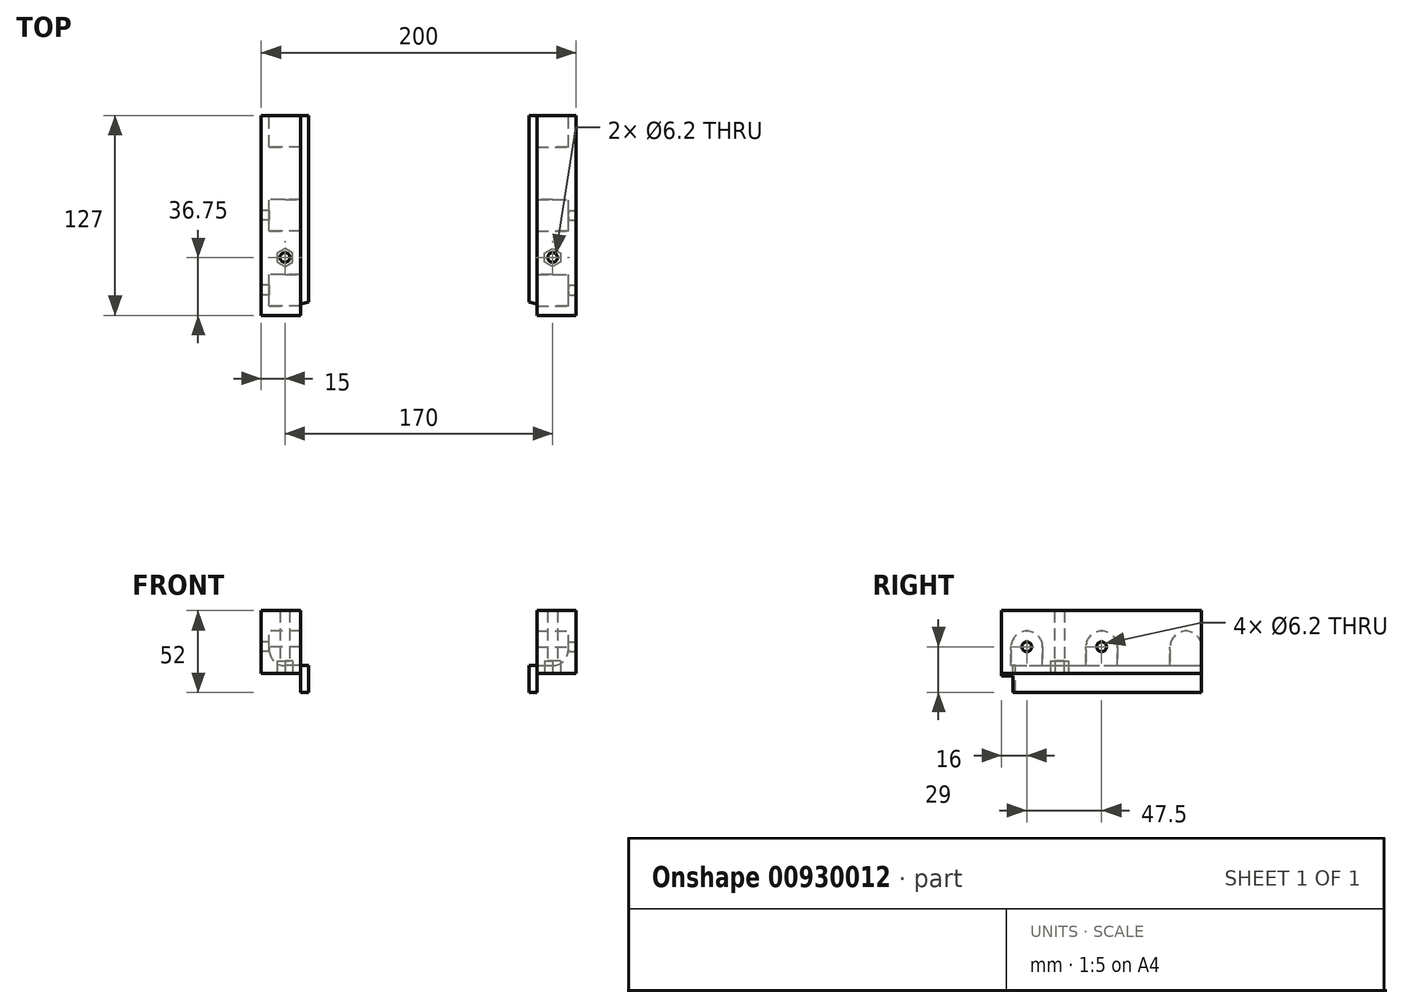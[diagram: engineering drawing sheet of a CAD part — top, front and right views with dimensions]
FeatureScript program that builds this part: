
annotation { "Feature Type Name" : "Feature", "Feature Type Description" : "" }
export const myFeature = defineFeature(function(context is Context, id is Id, definition is map)
    precondition{}
    {
        {
            var Q0;
            Q0=qCreatedBy(makeId("Front.planeOp"),FACE);
            var sketch = newSketch(context, id + "F0", { "sketchPlane" : qUnion([Q0])});
            skLineSegment(sketch, "E0", {"start": v(0, 40) * mm, "end": v(0, 0) * mm});
            skLineSegment(sketch, "E1", {"start": v(0, 0) * mm, "end": v(23.5, 0) * mm});
            skLineSegment(sketch, "E2", {"start": v(25, -1.5) * mm, "end": v(25, -12) * mm});
            skLineSegment(sketch, "E3", {"start": v(25, -12) * mm, "end": v(30, -12) * mm});
            skLineSegment(sketch, "E4", {"start": v(30, -12) * mm, "end": v(30, 5) * mm});
            skLineSegment(sketch, "E5", {"start": v(30, 5) * mm, "end": v(15, 5) * mm});
            skLineSegment(sketch, "E6", {"start": v(5, 15) * mm, "end": v(5, 40) * mm});
            skLineSegment(sketch, "E7", {"start": v(5, 40) * mm, "end": v(0, 40) * mm});
            skPoint(sketch, "E8.visualSharp", {"position": v(25, 0) * mm});
            skArc(sketch, "E8.filletArc", {"start": v(25, -1.5) * mm, "mid": v(24.56, -0.44) * mm, "end": v(23.5, 0) * mm});
            skPoint(sketch, "E9.visualSharp", {"position": v(5, 5) * mm});
            skArc(sketch, "E9.filletArc", {"start": v(5, 15) * mm, "mid": v(7.93, 7.93) * mm, "end": v(15, 5) * mm});
            skSolve(sketch);
        }
        {
            var Q0;
            Q0=makeQuery(id+"F0.imprint","IMPRINT",FACE,{"disambiguationData":[TD([[makeQuery(id+"F0.imprint","IMPRINT",EDGE,{"derivedFrom":sQuery(id+"F0.wireOp",EDGE,"E0")}),1.0]])]});
            extrude(context, id + "F1", {"entities" : qUnion([Q0]), "endBound" : BoundingType.SYMMETRIC, "depth" : 127 * mm, "offsetDistance" : 25 * mm});
        }
        {
            var Q0;
            Q0=makeQuery(id+"F1.opExtrude","SWEPT_FACE",FACE,{"disambiguationData":[OSD([sQuery(id+"F0.wireOp",EDGE,"E0")])]});
            var sketch = newSketch(context, id + "F2", { "sketchPlane" : qUnion([Q0])});
            skPoint(sketch, "E10", {"position": v(0, 17) * mm});
            skPoint(sketch, "E11", {"position": v(47.5, 17) * mm});
            skPoint(sketch, "E12", {"position": v(-53.5, 17) * mm});
            skSolve(sketch);
        }
        {
            var Q0;
            {var subQ0=sQuery(id+"F0.wireOp",EDGE,"E0");Q0=makeQuery(id+"F2.imprint","IMPRINT",FACE,{"disambiguationData":[TD([[makeQuery(id+"F2.imprint","IMPRINT",EDGE,{"derivedFrom":makeQuery(id+"F1.opExtrude","CAP_EDGE",EDGE,{"disambiguationData":[OSD([subQ0])],"isStart":true})}),1.0]])]});}
            var sketch = newSketch(context, id + "F3", { "sketchPlane" : qUnion([Q0])});
            skArc(sketch, "E13", {"start": v(-10, 17) * mm, "mid": v(0, 27) * mm, "end": v(10, 17) * mm});
            skArc(sketch, "E14", {"start": v(37.5, 17) * mm, "mid": v(47.5, 27) * mm, "end": v(57.5, 17) * mm});
            skLineSegment(sketch, "E15", {"start": v(-10, 17) * mm, "end": v(-10, 0) * mm});
            skLineSegment(sketch, "E16", {"start": v(-10, 0) * mm, "end": v(10, 0) * mm});
            skLineSegment(sketch, "E17", {"start": v(10, 0) * mm, "end": v(10, 17) * mm});
            skLineSegment(sketch, "E18", {"start": v(37.5, 17) * mm, "end": v(37.5, 0) * mm});
            skLineSegment(sketch, "E19", {"start": v(37.5, 0) * mm, "end": v(57.5, 0) * mm});
            skLineSegment(sketch, "E20", {"start": v(57.5, 0) * mm, "end": v(57.5, 17) * mm});
            skArc(sketch, "E21", {"start": v(-63.5, 17) * mm, "mid": v(-53.5, 27) * mm, "end": v(-43.5, 17) * mm});
            skLineSegment(sketch, "E22", {"start": v(-63.5, 17) * mm, "end": v(-63.5, 0) * mm});
            skLineSegment(sketch, "E23", {"start": v(-63.5, 0) * mm, "end": v(-43.5, 0) * mm});
            skLineSegment(sketch, "E24", {"start": v(-43.5, 0) * mm, "end": v(-43.5, 17) * mm});
            skSolve(sketch);
        }
        {
            var Q0;
            Q0=makeQuery(id+"F3.imprint","IMPRINT",FACE,{"disambiguationData":[TD([[makeQuery(id+"F3.imprint","IMPRINT",EDGE,{"derivedFrom":sQuery(id+"F3.wireOp",EDGE,"E14")}),-1.0]])]});
            var Q1;
            Q1=makeQuery(id+"F3.imprint","IMPRINT",FACE,{"disambiguationData":[TD([[makeQuery(id+"F3.imprint","IMPRINT",EDGE,{"derivedFrom":sQuery(id+"F3.wireOp",EDGE,"E13")}),-1.0]])]});
            var Q2;
            Q2=makeQuery(id+"F3.imprint","IMPRINT",FACE,{"disambiguationData":[TD([[makeQuery(id+"F3.imprint","IMPRINT",EDGE,{"derivedFrom":sQuery(id+"F3.wireOp",EDGE,"E21")}),-1.0]])]});
            var Q3;
            Q3=makeQuery(id+"F1.opExtrude","SWEPT_FACE",FACE,{"disambiguationData":[OSD([sQuery(id+"F0.wireOp",EDGE,"E4")])]});
            extrude(context, id + "F4", {"entities" : qUnion([Q0, Q1, Q2]), "operationType" : NewBodyOperationType.ADD, "oppositeDirection" : true, "depth" : 25 * mm, "endBoundEntityFace" : qUnion([Q3]), "offsetDistance" : 25 * mm});
        }
        {
            var Q0;
            Q0=sQuery(id+"F2.wireOp",VERTEX,"E10");
            var Q1;
            Q1=sQuery(id+"F2.wireOp",VERTEX,"E11");
            var Q2;
            Q2=makeQuery(id+"F1.opExtrude","SWEPT_BODY",BODY,{"disambiguationData":[OSD([sQuery(id+"F0.wireOp",EDGE,"E0"),sQuery(id+"F0.wireOp",EDGE,"E1"),sQuery(id+"F0.wireOp",EDGE,"E2"),sQuery(id+"F0.wireOp",EDGE,"E3"),sQuery(id+"F0.wireOp",EDGE,"E4"),sQuery(id+"F0.wireOp",EDGE,"E5"),sQuery(id+"F0.wireOp",EDGE,"E6"),sQuery(id+"F0.wireOp",EDGE,"E7"),sQuery(id+"F0.wireOp",EDGE,"E8.filletArc"),sQuery(id+"F0.wireOp",EDGE,"E9.filletArc")])]});
            hole(context, id + "F5", {"style" : HoleStyle.SIMPLE, "endStyle" : HoleEndStyle.THROUGH, "holeDiameter" : 6.2 * mm, "majorDiameter" : 5 * mm, "isTappedThrough" : true, "tappedDepth" : 12 * mm, "tapClearance" : 3, "locations" : qUnion([Q0, Q1]), "scope" : qUnion([Q2])});
        }
        {
            var Q0;
            Q0=makeQuery(id+"F1.opExtrude","SWEPT_FACE",FACE,{"disambiguationData":[OSD([sQuery(id+"F0.wireOp",EDGE,"E1")])]});
            var sketch = newSketch(context, id + "F6", { "sketchPlane" : qUnion([Q0])});
            skPoint(sketch, "E25", {"position": v(15, 26.75) * mm});
            skSolve(sketch);
        }
        {
            var Q0;
            {var subQ0=sQuery(id+"F0.wireOp",EDGE,"E1");Q0=makeQuery(id+"F6.imprint","IMPRINT",FACE,{"disambiguationData":[TD([[makeQuery(id+"F6.imprint","IMPRINT",EDGE,{"derivedFrom":makeQuery(id+"F1.opExtrude","CAP_EDGE",EDGE,{"disambiguationData":[OSD([subQ0])],"isStart":true})}),1.0]])]});}
            var sketch = newSketch(context, id + "F7", { "sketchPlane" : qUnion([Q0])});
            skArc(sketch, "E26", {"start": v(15, 16.75) * mm, "mid": v(25, 26.75) * mm, "end": v(15, 36.75) * mm});
            skLineSegment(sketch, "E27", {"start": v(15, 36.75) * mm, "end": v(0, 36.75) * mm});
            skLineSegment(sketch, "E28", {"start": v(0, 36.75) * mm, "end": v(0, 16.75) * mm});
            skLineSegment(sketch, "E29", {"start": v(0, 16.75) * mm, "end": v(15, 16.75) * mm});
            skSolve(sketch);
        }
        {
            var Q0;
            {var subQ0=sQuery(id+"F7.wireOp",EDGE,"E27");Q0=makeQuery(id+"F7.imprint","IMPRINT",FACE,{"disambiguationData":[TD([[makeQuery(id+"F7.imprint","IMPRINT",EDGE,{"derivedFrom":subQ0}),1.0]])]});}
            var Q1;
            {var subQ0=sQuery(id+"F7.wireOp",EDGE,"E26");var subQ1=makeQuery(id+"F6.imprint","IMPRINT",EDGE,{"derivedFrom":makeQuery(id+"F4.boolean.opBoolean","INTERSECT",EDGE,{"derivedFrom":[makeQuery(id+"F4.opExtrude","SWEPT_FACE",FACE,{"disambiguationData":[OSD([sQuery(id+"F3.wireOp",EDGE,"E16")])]}),makeQuery(id+"F4.opExtrude","SWEPT_FACE",FACE,{"disambiguationData":[OSD([sQuery(id+"F3.wireOp",EDGE,"E19")])]})]})});var subQ2=makeQuery(id+"F7.imprint","INTERSECT",VERTEX,{"disambiguationData":[OD(0.0)],"derivedFrom":[subQ1,subQ0]});Q1=makeQuery(id+"F7.imprint","IMPRINT",FACE,{"disambiguationData":[TD([[makeQuery(id+"F7.imprint","IMPRINT",EDGE,{"disambiguationData":[TD([[subQ2,-1.0]])],"derivedFrom":subQ0}),1.0]])]});}
            var Q2;
            Q2=makeQuery(id+"F1.opExtrude","SWEPT_FACE",FACE,{"disambiguationData":[OSD([sQuery(id+"F0.wireOp",EDGE,"E7")])]});
            extrude(context, id + "F8", {"entities" : qUnion([Q0, Q1]), "operationType" : NewBodyOperationType.ADD, "oppositeDirection" : true, "depth" : 30 * mm, "endBoundEntityFace" : qUnion([Q2]), "offsetDistance" : 25 * mm});
        }
        {
            var Q0;
            Q0=sQuery(id+"F6.wireOp",VERTEX,"E25");
            var Q1;
            Q1=makeQuery(id+"F1.opExtrude","SWEPT_BODY",BODY,{"disambiguationData":[OSD([sQuery(id+"F0.wireOp",EDGE,"E0"),sQuery(id+"F0.wireOp",EDGE,"E1"),sQuery(id+"F0.wireOp",EDGE,"E2"),sQuery(id+"F0.wireOp",EDGE,"E3"),sQuery(id+"F0.wireOp",EDGE,"E4"),sQuery(id+"F0.wireOp",EDGE,"E5"),sQuery(id+"F0.wireOp",EDGE,"E6"),sQuery(id+"F0.wireOp",EDGE,"E7"),sQuery(id+"F0.wireOp",EDGE,"E8.filletArc"),sQuery(id+"F0.wireOp",EDGE,"E9.filletArc")])]});
            hole(context, id + "F9", {"style" : HoleStyle.SIMPLE, "endStyle" : HoleEndStyle.THROUGH, "holeDiameter" : 6.2 * mm, "majorDiameter" : 5 * mm, "isTappedThrough" : true, "tappedDepth" : 12 * mm, "tapClearance" : 3, "locations" : qUnion([Q0]), "scope" : qUnion([Q1])});
        }
        {
            var Q0;
            {var subQ0=sQuery(id+"F0.wireOp",EDGE,"E1");Q0=makeQuery(id+"F6.imprint","IMPRINT",FACE,{"disambiguationData":[TD([[makeQuery(id+"F6.imprint","IMPRINT",EDGE,{"derivedFrom":makeQuery(id+"F1.opExtrude","CAP_EDGE",EDGE,{"disambiguationData":[OSD([subQ0])],"isStart":true})}),1.0]])]});}
            var sketch = newSketch(context, id + "F10", { "sketchPlane" : qUnion([Q0])});
            skCircle(sketch, "E30.cCircle", {"center": v(15, 26.75) * mm, "radius": 5 * mm, "construction": true});
            skLineSegment(sketch, "E30.0", {"start": v(20, 23.86) * mm, "end": v(15, 20.98) * mm});
            skLineSegment(sketch, "E30.1", {"start": v(15, 20.98) * mm, "end": v(10, 23.86) * mm});
            skLineSegment(sketch, "E30.2", {"start": v(10, 23.86) * mm, "end": v(10, 29.64) * mm});
            skLineSegment(sketch, "E30.3", {"start": v(10, 29.64) * mm, "end": v(15, 32.52) * mm});
            skLineSegment(sketch, "E30.4", {"start": v(15, 32.52) * mm, "end": v(20, 29.64) * mm});
            skLineSegment(sketch, "E30.5", {"start": v(20, 29.64) * mm, "end": v(20, 23.86) * mm});
            skPoint(sketch, "E30.0.midPoint", {"position": v(17.5, 22.42) * mm});
            skSolve(sketch);
        }
        {
            var Q0;
            Q0=makeQuery(id+"F10.imprint","IMPRINT",FACE,{"disambiguationData":[TD([[makeQuery(id+"F10.imprint","IMPRINT",EDGE,{"derivedFrom":sQuery(id+"F10.wireOp",EDGE,"E30.0")}),-1.0]])]});
            var Q1;
            Q1=makeQuery(id+"F10.imprint","IMPRINT",FACE,{"disambiguationData":[TD([[makeQuery(id+"F10.imprint","IMPRINT",EDGE,{"derivedFrom":sQuery(id+"F10.wireOp",EDGE,"dd04fbf3-1c94-40b8-9f44-460d01ebb8ad.0")}),-1.0]])]});
            extrude(context, id + "F11", {"entities" : qUnion([Q0, Q1]), "operationType" : NewBodyOperationType.REMOVE, "oppositeDirection" : true, "depth" : 8 * mm, "offsetDistance" : 25 * mm});
        }
        {
            var Q0;
            Q0=qCreatedBy(makeId("Right.planeOp"),FACE);
            cPlane(context, id + "F12", {"entities" : qUnion([Q0]), "cplaneType" : CPlaneType.OFFSET, "offset" : 100 * mm, "width" : 150 * mm, "height" : 150 * mm});
        }
        {
            var Q0;
            Q0=makeQuery(id+"F1.opExtrude","SWEPT_FACE",FACE,{"disambiguationData":[OSD([sQuery(id+"F0.wireOp",EDGE,"E7")])]});
            var sketch = newSketch(context, id + "F13", { "sketchPlane" : qUnion([Q0])});
            skLineSegment(sketch, "E31", {"start": v(0, -63.5) * mm, "end": v(40, -52.03) * mm});
            skLineSegment(sketch, "E32", {"start": v(40, -52.03) * mm, "end": v(40, -63.5) * mm});
            skLineSegment(sketch, "E33", {"start": v(40, -63.5) * mm, "end": v(0, -63.5) * mm});
            skSolve(sketch);
        }
        {
            var Q0;
            {var subQ0=sQuery(id+"F13.wireOp",EDGE,"E32");Q0=makeQuery(id+"F13.imprint","IMPRINT",FACE,{"disambiguationData":[TD([[makeQuery(id+"F13.imprint","IMPRINT",EDGE,{"derivedFrom":subQ0}),-1.0]])]});}
            extrude(context, id + "F14", {"entities" : qUnion([Q0]), "operationType" : NewBodyOperationType.REMOVE, "endBound" : BoundingType.THROUGH_ALL, "oppositeDirection" : true, "depth" : 25 * mm, "offsetDistance" : 25 * mm});
        }
        {
            var Q0;
            Q0=makeQuery(id+"F1.opExtrude","SWEPT_BODY",BODY,{"disambiguationData":[OSD([sQuery(id+"F0.wireOp",EDGE,"E0"),sQuery(id+"F0.wireOp",EDGE,"E1"),sQuery(id+"F0.wireOp",EDGE,"E2"),sQuery(id+"F0.wireOp",EDGE,"E3"),sQuery(id+"F0.wireOp",EDGE,"E4"),sQuery(id+"F0.wireOp",EDGE,"E5"),sQuery(id+"F0.wireOp",EDGE,"E6"),sQuery(id+"F0.wireOp",EDGE,"E7"),sQuery(id+"F0.wireOp",EDGE,"E8.filletArc"),sQuery(id+"F0.wireOp",EDGE,"E9.filletArc")])]});
            var Q1;
            Q1=qCreatedBy(id+"F12.planeOp",FACE);
            mirror(context, id + "F15", {"entities" : qUnion([Q0]), "mirrorPlane" : qUnion([Q1])});
        }
    });
